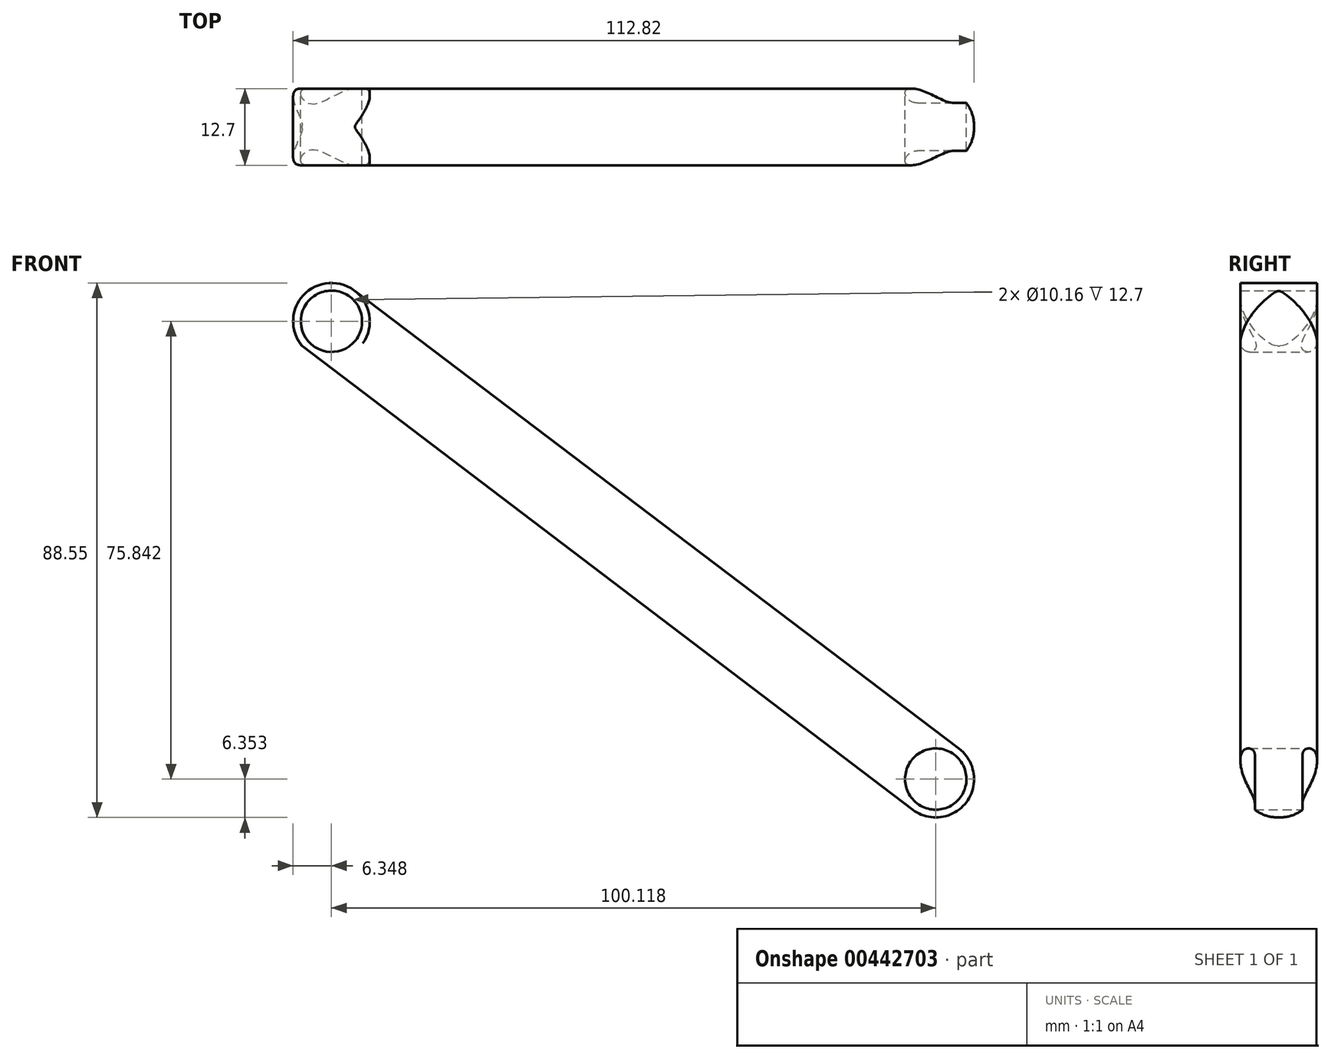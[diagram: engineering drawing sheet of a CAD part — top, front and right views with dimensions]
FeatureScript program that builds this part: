
annotation { "Feature Type Name" : "Feature", "Feature Type Description" : "" }
export const myFeature = defineFeature(function(context is Context, id is Id, definition is map)
    precondition{}
    {
        {
            var Q0;
            Q0=qCreatedBy(makeId("Front.planeOp"),FACE);
            var sketch = newSketch(context, id + "F0", { "sketchPlane" : qUnion([Q0])});
            skCircle(sketch, "E0", {"center": v(-79.64, 55.56) * mm, "radius": 6.35 * mm});
            skCircle(sketch, "E1", {"center": v(20.48, -20.29) * mm, "radius": 6.35 * mm});
            skLineSegment(sketch, "E2", {"start": v(-84.5, 51.47) * mm, "end": v(16.64, -25.34) * mm});
            skLineSegment(sketch, "E3", {"start": v(-75.7, 60.54) * mm, "end": v(24.31, -15.23) * mm});
            skCircle(sketch, "E4", {"center": v(-79.64, 55.56) * mm, "radius": 5.08 * mm});
            skCircle(sketch, "E5", {"center": v(20.48, -20.29) * mm, "radius": 5.08 * mm});
            skSolve(sketch);
        }
        {
            var Q0;
            Q0=makeQuery(id+"F0.imprint","IMPRINT",FACE,{"disambiguationData":[TD([[makeQuery(id+"F0.imprint","IMPRINT",EDGE,{"derivedFrom":sQuery(id+"F0.wireOp",EDGE,"E4")}),-1.0]])]});
            var Q1;
            Q1=makeQuery(id+"F0.imprint","IMPRINT",FACE,{"disambiguationData":[TD([[makeQuery(id+"F0.imprint","IMPRINT",EDGE,{"derivedFrom":sQuery(id+"F0.wireOp",EDGE,"E5")}),-1.0]])]});
            var Q2;
            {var subQ0=sQuery(id+"F0.wireOp",EDGE,"E3");Q2=makeQuery(id+"F0.imprint","IMPRINT",FACE,{"disambiguationData":[TD([[makeQuery(id+"F0.imprint","IMPRINT",EDGE,{"derivedFrom":subQ0}),-1.0]])]});}
            extrude(context, id + "F1", {"entities" : qUnion([Q0, Q1, Q2]), "depth" : 12.7 * mm});
        }
        {
            var Q0;
            Q0=makeQuery(id+"F1.opExtrude","CAP_EDGE",EDGE,{"disambiguationData":[OSD([sQuery(id+"F0.wireOp",EDGE,"E3")])],"isStart":false});
            var Q1;
            Q1=makeQuery(id+"F1.opExtrude","CAP_EDGE",EDGE,{"disambiguationData":[OSD([sQuery(id+"F0.wireOp",EDGE,"E3")])],"isStart":true});
            var Q2;
            Q2=makeQuery(id+"F1.opExtrude","CAP_EDGE",EDGE,{"disambiguationData":[OSD([sQuery(id+"F0.wireOp",EDGE,"E2")])],"isStart":true});
            var Q3;
            Q3=makeQuery(id+"F1.opExtrude","CAP_EDGE",EDGE,{"disambiguationData":[OSD([sQuery(id+"F0.wireOp",EDGE,"E2")])],"isStart":false});
            fillet(context, id + "F2", {"entities" : qUnion([Q0, Q1, Q2, Q3]), "radius" : 6.13 * mm, "tangentPropagation" : true, "allowEdgeOverflow" : false});
        }
    });
